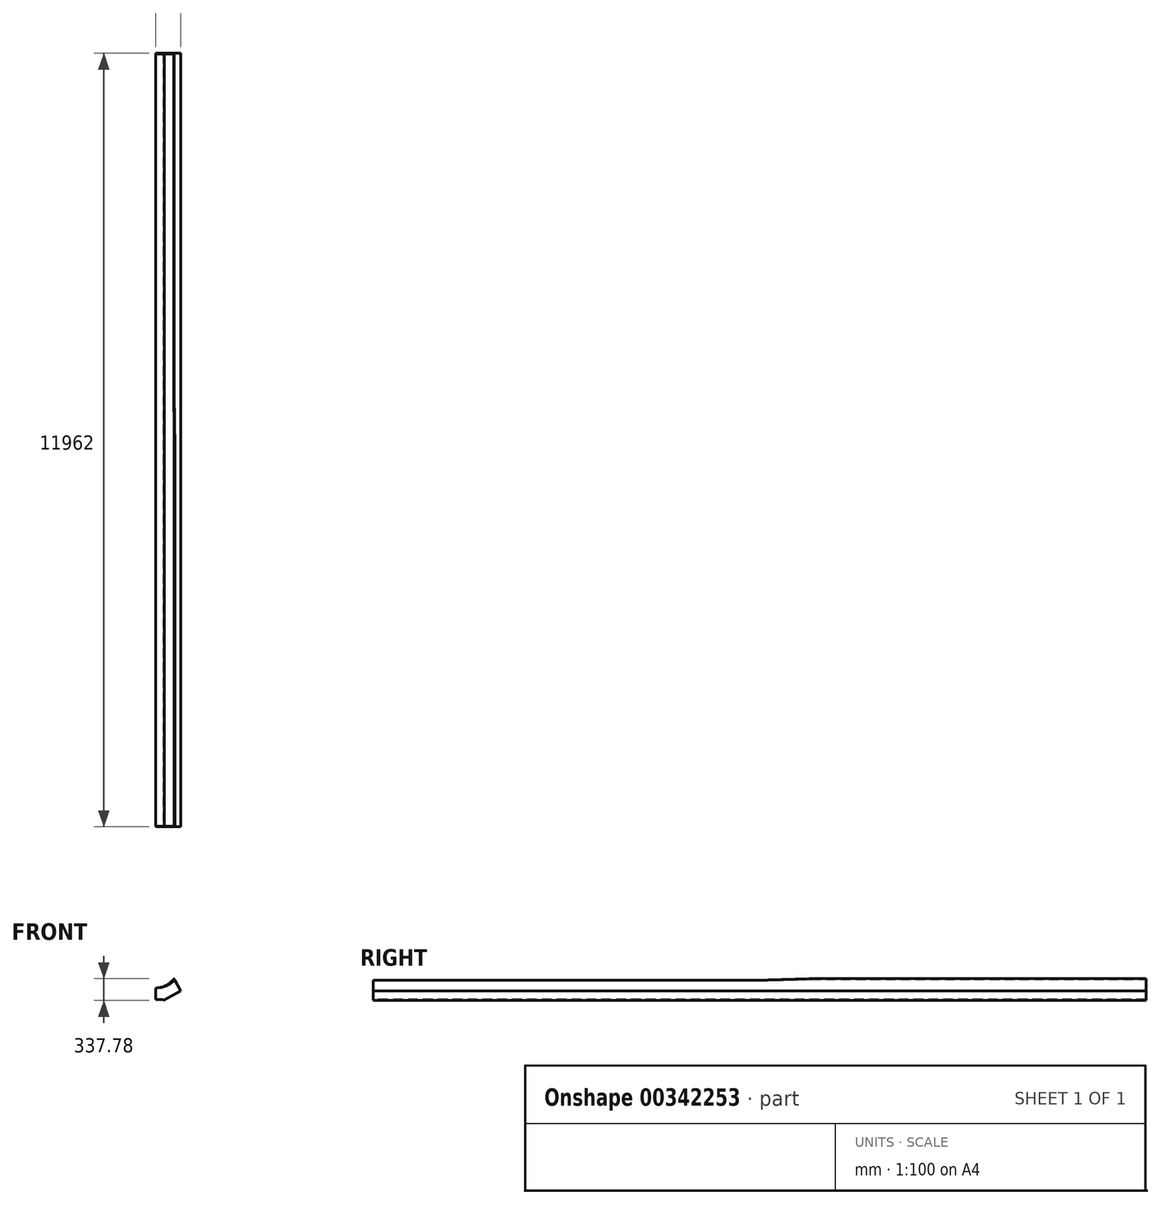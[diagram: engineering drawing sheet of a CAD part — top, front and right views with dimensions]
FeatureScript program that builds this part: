
annotation { "Feature Type Name" : "Feature", "Feature Type Description" : "" }
export const myFeature = defineFeature(function(context is Context, id is Id, definition is map)
    precondition{}
    {
        {
            var Q0;
            Q0=qCreatedBy(makeId("Front.planeOp"),FACE);
            cPlane(context, id + "F0", {"entities" : qUnion([Q0]), "cplaneType" : CPlaneType.OFFSET, "offset" : 119 * mm, "oppositeDirection" : true, "width" : 150 * mm, "height" : 150 * mm});
        }
        {
            var Q0;
            Q0=qCreatedBy(id+"F0.planeOp",FACE);
            var sketch = newSketch(context, id + "F1", { "sketchPlane" : qUnion([Q0])});
            skCircle(sketch, "E0", {"center": v(0, 0) * mm, "radius": 431.8 * mm, "construction": true});
            skLineSegment(sketch, "E1", {"start": v(0, 509.68) * mm, "end": v(0, -737.68) * mm, "construction": true});
            skLineSegment(sketch, "E2", {"start": v(0, -611.8) * mm, "end": v(117.96, -611.8) * mm});
            skLineSegment(sketch, "E3", {"start": v(117.96, -611.8) * mm, "end": v(125.72, -625.8) * mm});
            skLineSegment(sketch, "E4", {"start": v(125.72, -625.8) * mm, "end": v(391.28, -478.6) * mm});
            skLineSegment(sketch, "E5", {"start": v(0, -611.8) * mm, "end": v(0, -601.8) * mm});
            skLineSegment(sketch, "E6", {"start": v(0, -601.8) * mm, "end": v(136, -601.8) * mm});
            skLineSegment(sketch, "E7", {"start": v(136, -601.8) * mm, "end": v(374.77, -469.45) * mm});
            skLineSegment(sketch, "E8", {"start": v(391.28, -478.6) * mm, "end": v(0, 227.28) * mm});
            skLineSegment(sketch, "E9", {"start": v(374.77, -469.45) * mm, "end": v(0, 206.65) * mm});
            skLineSegment(sketch, "E10", {"start": v(0, 206.65) * mm, "end": v(0, 227.28) * mm});
            skSolve(sketch);
        }
        {
            var Q0;
            Q0 = qSketchRegion(id + "F1", true);
            extrude(context, id + "F2", {"entities" : qUnion([Q0]), "oppositeDirection" : true, "depth" : 11962 * mm});
        }
        {
            var Q0;
            Q0=makeQuery(id+"F2.opExtrude","SWEPT_BODY",BODY,{"disambiguationData":[OSD([sQuery(id+"F1.wireOp",EDGE,"E2"),sQuery(id+"F1.wireOp",EDGE,"E3"),sQuery(id+"F1.wireOp",EDGE,"E4"),sQuery(id+"F1.wireOp",EDGE,"zi3JzrBy-5Q1e-MdjT-Vtr0-5VZ5DObRVNgf"),sQuery(id+"F1.wireOp",EDGE,"E5"),sQuery(id+"F1.wireOp",EDGE,"E6"),sQuery(id+"F1.wireOp",EDGE,"E7"),sQuery(id+"F1.wireOp",EDGE,"hqveH5RQ-Cihz-fbub-OvEs-BpCpdZSg4RGn"),sQuery(id+"F1.wireOp",EDGE,"gFo7uHAR-rxPM-XtB8-UGly-YZvbTqmEu5O6")])]});
            var Q1;
            Q1=qCreatedBy(makeId("Right.planeOp"),FACE);
            mirror(context, id + "F3", {"operationType" : NewBodyOperationType.ADD, "entities" : qUnion([Q0]), "mirrorPlane" : qUnion([Q1])});
        }
        {
            var Q0;
            Q0=qCreatedBy(id+"F0.planeOp",FACE);
            var sketch = newSketch(context, id + "F4", { "sketchPlane" : qUnion([Q0])});
            skLineSegment(sketch, "E11.0", {"start": v(374.77, -469.45) * mm, "end": v(0, 206.65) * mm});
            skLineSegment(sketch, "E12.0", {"start": v(-374.77, -469.45) * mm, "end": v(0, 206.65) * mm});
            skLineSegment(sketch, "E13.0", {"start": v(-136, -601.8) * mm, "end": v(-374.77, -469.45) * mm});
            skLineSegment(sketch, "E14.0", {"start": v(-136, -601.8) * mm, "end": v(136, -601.8) * mm});
            skLineSegment(sketch, "E15.0", {"start": v(136, -601.8) * mm, "end": v(374.77, -469.45) * mm});
            skSolve(sketch);
        }
        {
            var Q0;
            Q0=qCreatedBy(makeId("Front.planeOp"),FACE);
            cPlane(context, id + "F5", {"entities" : qUnion([Q0]), "cplaneType" : CPlaneType.OFFSET, "offset" : 12081 * mm, "oppositeDirection" : true, "width" : 150 * mm, "height" : 150 * mm});
        }
        {
            var Q0;
            Q0=qCreatedBy(id+"F5.planeOp",FACE);
            var sketch = newSketch(context, id + "F6", { "sketchPlane" : qUnion([Q0])});
            skLineSegment(sketch, "E16.0.0", {"start": v(-136, -601.8) * mm, "end": v(136, -601.8) * mm});
            skLineSegment(sketch, "E16.0.1", {"start": v(136, -601.8) * mm, "end": v(374.77, -469.45) * mm});
            skLineSegment(sketch, "E16.0.2", {"start": v(374.77, -469.45) * mm, "end": v(0, 206.65) * mm});
            skLineSegment(sketch, "E16.0.3", {"start": v(0, 206.65) * mm, "end": v(-374.77, -469.45) * mm});
            skLineSegment(sketch, "E16.0.4", {"start": v(-374.77, -469.45) * mm, "end": v(-136, -601.8) * mm});
            skSolve(sketch);
        }
        {
            var Q0;
            Q0 = qSketchRegion(id + "F4", true);
            extrude(context, id + "F7", {"entities" : qUnion([Q0]), "operationType" : NewBodyOperationType.ADD, "oppositeDirection" : true, "depth" : 10 * mm});
        }
        {
            var Q0;
            Q0 = qSketchRegion(id + "F6", true);
            extrude(context, id + "F8", {"entities" : qUnion([Q0]), "depth" : 10 * mm});
        }
        {
            var Q0;
            Q0=qCreatedBy(makeId("Front.planeOp"),FACE);
            cPlane(context, id + "F9", {"entities" : qUnion([Q0]), "cplaneType" : CPlaneType.OFFSET, "offset" : 6100 * mm, "oppositeDirection" : true, "width" : 150 * mm, "height" : 150 * mm});
        }
        {
            var Q0;
            Q0=qCreatedBy(makeId("Front.planeOp"),FACE);
            cPlane(context, id + "F10", {"entities" : qUnion([Q0]), "cplaneType" : CPlaneType.OFFSET, "offset" : 6900 * mm, "oppositeDirection" : true, "width" : 150 * mm, "height" : 150 * mm});
        }
        {
            var Q0;
            Q0=qCreatedBy(makeId("Front.planeOp"),FACE);
            cPlane(context, id + "F11", {"entities" : qUnion([Q0]), "cplaneType" : CPlaneType.OFFSET, "offset" : 12200 * mm, "oppositeDirection" : true, "width" : 150 * mm, "height" : 150 * mm});
        }
        {
            var Q0;
            Q0=qCreatedBy(makeId("Front.planeOp"),FACE);
            var sketch = newSketch(context, id + "F12", { "sketchPlane" : qUnion([Q0])});
            skCircle(sketch, "E17", {"center": v(0, 0) * mm, "radius": 431.8 * mm});
            skSolve(sketch);
        }
        {
            var Q0;
            Q0=qCreatedBy(id+"F9.planeOp",FACE);
            var sketch = newSketch(context, id + "F13", { "sketchPlane" : qUnion([Q0])});
            skCircle(sketch, "E18", {"center": v(0, 0) * mm, "radius": 431.8 * mm});
            skSolve(sketch);
        }
        {
            var Q0;
            Q0=qCreatedBy(id+"F10.planeOp",FACE);
            var sketch = newSketch(context, id + "F14", { "sketchPlane" : qUnion([Q0])});
            skCircle(sketch, "E19", {"center": v(0, -76.2) * mm, "radius": 355.6 * mm});
            skSolve(sketch);
        }
        {
            var Q0;
            Q0=qCreatedBy(id+"F11.planeOp",FACE);
            var sketch = newSketch(context, id + "F15", { "sketchPlane" : qUnion([Q0])});
            skCircle(sketch, "E20", {"center": v(0, -76.2) * mm, "radius": 355.6 * mm});
            skSolve(sketch);
        }
        {
            var Q0;
            Q0=makeQuery(id+"F12.imprint","IMPRINT",FACE,{"disambiguationData":[TD([[makeQuery(id+"F12.imprint","IMPRINT",EDGE,{"derivedFrom":sQuery(id+"F12.wireOp",EDGE,"E17")}),1.0]])]});
            extrude(context, id + "F16", {"entities" : qUnion([Q0]), "operationType" : NewBodyOperationType.REMOVE, "oppositeDirection" : true, "depth" : 6100 * mm});
        }
        {
            var Q0;
            Q0=makeQuery(id+"F15.imprint","IMPRINT",FACE,{"disambiguationData":[TD([[makeQuery(id+"F15.imprint","IMPRINT",EDGE,{"derivedFrom":sQuery(id+"F15.wireOp",EDGE,"E20")}),1.0]])]});
            extrude(context, id + "F17", {"entities" : qUnion([Q0]), "operationType" : NewBodyOperationType.REMOVE, "depth" : 5300 * mm});
        }
        {
            var Q1;
            Q1=makeQuery(id+"F13.imprint","IMPRINT",FACE,{"disambiguationData":[TD([[makeQuery(id+"F13.imprint","IMPRINT",EDGE,{"derivedFrom":sQuery(id+"F13.wireOp",EDGE,"E18")}),1.0]])]});
            var Q2;
            Q2=makeQuery(id+"F14.imprint","IMPRINT",FACE,{"disambiguationData":[TD([[makeQuery(id+"F14.imprint","IMPRINT",EDGE,{"derivedFrom":sQuery(id+"F14.wireOp",EDGE,"E19")}),1.0]])]});
            loft(context, id + "F18", {"operationType" : NewBodyOperationType.REMOVE, "sheetProfilesArray" : [{ "sheetProfileEntities" : qUnion([Q1]) }, { "sheetProfileEntities" : qUnion([Q2]) }]});
        }
        {
            var Q0;
            Q0=qCreatedBy(makeId("Right.planeOp"),FACE);
            var sketch = newSketch(context, id + "F19", { "sketchPlane" : qUnion([Q0])});
            skLineSegment(sketch, "E21.bottom", {"start": v(-225.26, 468.7) * mm, "end": v(12328.73, 468.7) * mm});
            skLineSegment(sketch, "E21.top", {"start": v(-225.26, -1374.12) * mm, "end": v(12328.73, -1374.12) * mm});
            skLineSegment(sketch, "E21.left", {"start": v(-225.26, 468.7) * mm, "end": v(-225.26, -1374.12) * mm});
            skLineSegment(sketch, "E21.right", {"start": v(12328.73, 468.7) * mm, "end": v(12328.73, -1374.12) * mm});
            skSolve(sketch);
        }
        {
            var Q0;
            Q0=makeQuery(id+"F19.imprint","IMPRINT",FACE,{"disambiguationData":[TD([[makeQuery(id+"F19.imprint","IMPRINT",EDGE,{"derivedFrom":sQuery(id+"F19.wireOp",EDGE,"E21.bottom")}),-1.0]])]});
            extrude(context, id + "F20", {"entities" : qUnion([Q0]), "operationType" : NewBodyOperationType.REMOVE, "oppositeDirection" : true, "depth" : 2000 * mm});
        }
    });
